# Revit family: CHWC105 Chartham Rimless 700 BTW Rev01 OK
name_source: partatom
category: Generic Models
revit_build: Autodesk Revit 2015 (Build: 20140606_1530(x64)
units: mm (PartAtom-declared; Revit-internal decimal feet)

## types (1)
- SWC_WC_CHWC105
    Brand = SanCeram
    Help = http://www.theswc.co.uk
    Manufacturer URL = www.theswc.co.uk
    NBS Reference Code = N13 - 300
    NBS Reference Description = WCS AND CISTERNS
    Name = Chartham Rimless 700 back to wall WC
    Nominal Height = 455 mm
    Nominal Length = 700 mm
    Nominal Width = 365 mm
    Pan Mounting = Back to Wall
    Primary Finishes = Alpine White
    Primary Material = Vitreous China
    Product Family = Sanitary
    Product Group = Back to Wall WC
    Product Information = http://www.theswc.co.uk
    Product SKU = CHWC105
    Rim Type = Rimless
    Seat = Seat only white - CHWC112 / Seat only Blue - CHWC113/ Seat only Grey - CHWC114 (Supplied seperatly)
    Seat Colour = White/ Blue/ Grey
    Secondary Material = Polished Chrome
    Spare Parts = http://www.theswc.co.uk
    Trap Type = P Trap
    Trapway Tap = Concealed
    Waste Height = 190 mm
    Weight = 34kg

## geometry (parser evidence)
native form markers: Blend x2, Sweep x2
no freeform markers — native parametric forms only
